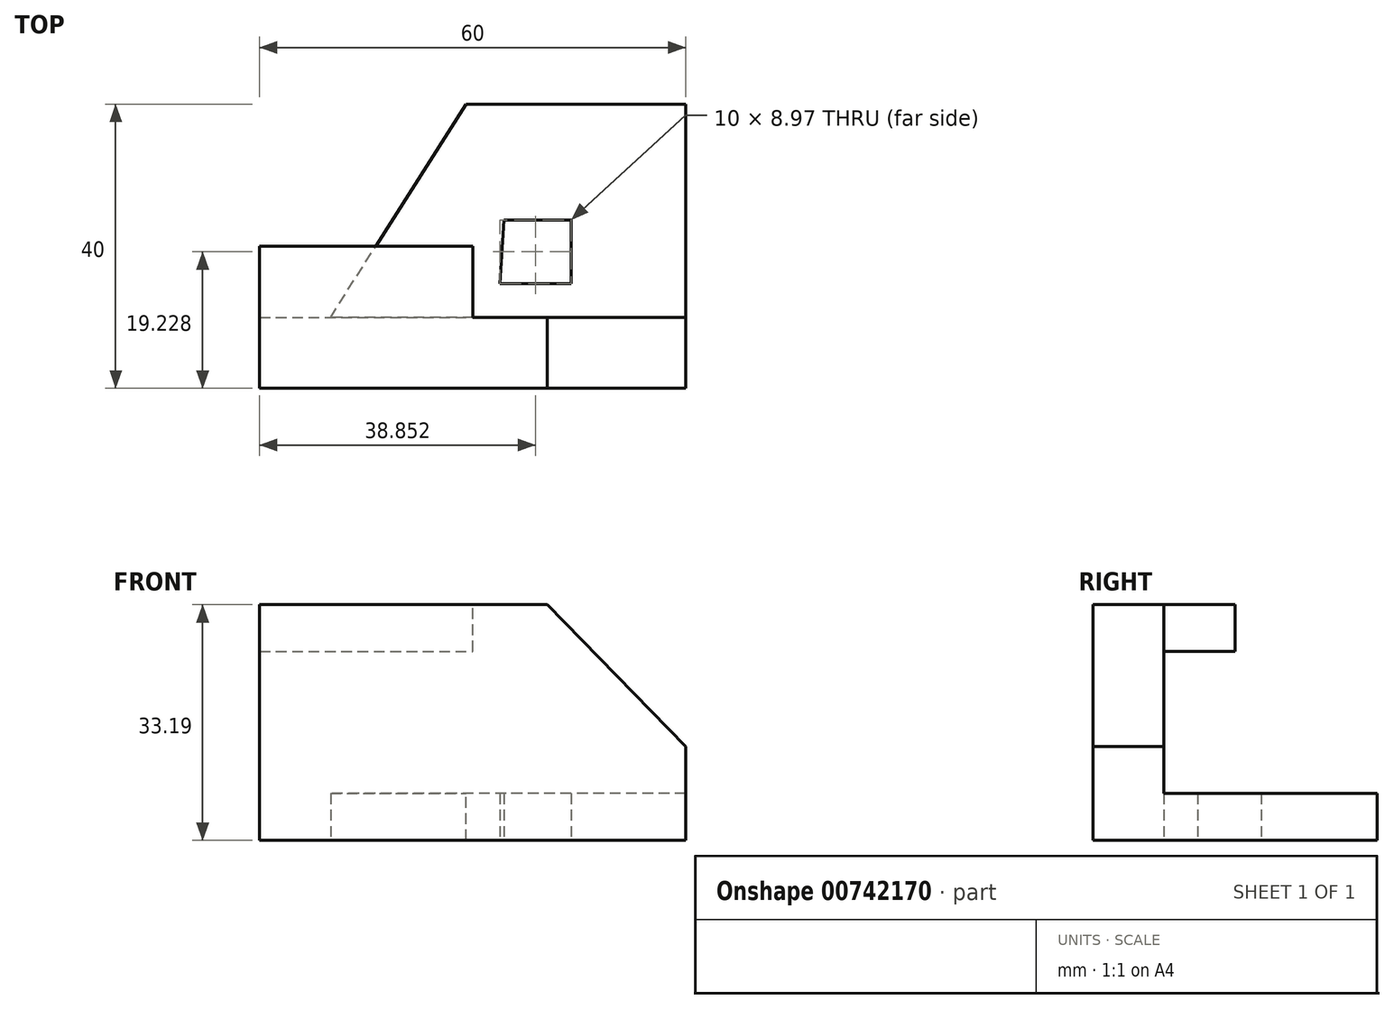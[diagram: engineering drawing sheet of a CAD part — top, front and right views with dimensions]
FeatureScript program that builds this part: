
annotation { "Feature Type Name" : "Feature", "Feature Type Description" : "" }
export const myFeature = defineFeature(function(context is Context, id is Id, definition is map)
    precondition{}
    {
        {
            var Q0;
            Q0=qCreatedBy(makeId("Front.planeOp"),FACE);
            var sketch = newSketch(context, id + "F0", { "sketchPlane" : qUnion([Q0])});
            skLineSegment(sketch, "E0", {"start": v(0, 0) * mm, "end": v(-60, 0) * mm});
            skLineSegment(sketch, "E1", {"start": v(-60, 0) * mm, "end": v(-60, -33.19) * mm});
            skLineSegment(sketch, "E2", {"start": v(-60, -33.19) * mm, "end": v(0, -33.19) * mm});
            skLineSegment(sketch, "E3", {"start": v(0, -33.19) * mm, "end": v(0, 0) * mm});
            skSolve(sketch);
        }
        {
            var Q0;
            Q0=makeQuery(id+"F0.imprint","IMPRINT",FACE,{"disambiguationData":[TD([[makeQuery(id+"F0.imprint","IMPRINT",EDGE,{"derivedFrom":sQuery(id+"F0.wireOp",EDGE,"E0")}),1.0]])]});
            extrude(context, id + "F1", {"entities" : qUnion([Q0]), "depth" : 40 * mm, "offsetDistance" : 25.4 * mm});
        }
        {
            var Q0;
            Q0=qCreatedBy(makeId("Front.planeOp"),FACE);
            var sketch = newSketch(context, id + "F2", { "sketchPlane" : qUnion([Q0])});
            skLineSegment(sketch, "E4", {"start": v(0, 0) * mm, "end": v(-19.51, 0) * mm});
            skLineSegment(sketch, "E5", {"start": v(0, 0) * mm, "end": v(0, -20) * mm});
            skLineSegment(sketch, "E6", {"start": v(-19.51, 0) * mm, "end": v(0, -20) * mm});
            skSolve(sketch);
        }
        {
            var Q0;
            Q0=makeQuery(id+"F2.imprint","IMPRINT",FACE,{"disambiguationData":[TD([[makeQuery(id+"F2.imprint","IMPRINT",EDGE,{"derivedFrom":sQuery(id+"F2.wireOp",EDGE,"E4")}),1.0]])]});
            extrude(context, id + "F3", {"entities" : qUnion([Q0]), "operationType" : NewBodyOperationType.REMOVE, "depth" : 41.9 * mm, "offsetDistance" : 25.4 * mm});
        }
        {
            var Q0;
            Q0=makeQuery(id+"F1.opExtrude","CAP_FACE",FACE,{"disambiguationData":[OSD([sQuery(id+"F0.wireOp",EDGE,"E0"),sQuery(id+"F0.wireOp",EDGE,"E1"),sQuery(id+"F0.wireOp",EDGE,"E2"),sQuery(id+"F0.wireOp",EDGE,"E3")])],"isStart":true});
            var sketch = newSketch(context, id + "F4", { "sketchPlane" : qUnion([Q0])});
            skLineSegment(sketch, "E7", {"start": v(0, -26.6) * mm, "end": v(50, -26.6) * mm});
            skLineSegment(sketch, "E8", {"start": v(50, -26.6) * mm, "end": v(50, -33.19) * mm});
            skLineSegment(sketch, "E9", {"start": v(50, -33.19) * mm, "end": v(60, -33.19) * mm});
            skLineSegment(sketch, "E10", {"start": v(60, -33.19) * mm, "end": v(60, -6.58) * mm});
            skPoint(sketch, "E11.endSnap0", {"position": v(60, -19.89) * mm});
            skLineSegment(sketch, "E12", {"start": v(60, -6.58) * mm, "end": v(30, -6.58) * mm});
            skLineSegment(sketch, "E13", {"start": v(30, -6.58) * mm, "end": v(30, 0) * mm});
            skSolve(sketch);
        }
        {
            var Q0;
            {var subQ2=sQuery(id+"F4.wireOp",EDGE,"E7");Q0=makeQuery(id+"F4.imprint","IMPRINT",FACE,{"disambiguationData":[TD([[makeQuery(id+"F4.imprint","IMPRINT",EDGE,{"derivedFrom":subQ2}),1.0]])]});}
            extrude(context, id + "F5", {"entities" : qUnion([Q0]), "operationType" : NewBodyOperationType.REMOVE, "oppositeDirection" : true, "depth" : 30 * mm, "offsetDistance" : 25.4 * mm});
        }
        {
            var Q0;
            {var subQ0=sQuery(id+"F0.wireOp",EDGE,"E0");var subQ1=sQuery(id+"F0.wireOp",EDGE,"E1");Q0=makeQuery(id+"F5.boolean.opBoolean","SPLIT",FACE,{"disambiguationData":[TD([makeQuery(id+"F1.opExtrude","SWEPT_FACE",FACE,{"disambiguationData":[OSD([subQ0])]})])],"derivedFrom":makeQuery(id+"F1.opExtrude","CAP_FACE",FACE,{"disambiguationData":[OSD([subQ0,subQ1,sQuery(id+"F0.wireOp",EDGE,"E2"),sQuery(id+"F0.wireOp",EDGE,"E3")])],"isStart":true})});}
            extrude(context, id + "F6", {"entities" : qUnion([Q0]), "operationType" : NewBodyOperationType.REMOVE, "oppositeDirection" : true, "depth" : 20 * mm, "offsetDistance" : 25.4 * mm});
        }
        {
            var Q0;
            Q0=makeQuery(id+"F5.boolean.opBoolean","COPY",FACE,{"derivedFrom":makeQuery(id+"F5.opExtrude","SWEPT_FACE",FACE,{"disambiguationData":[OSD([sQuery(id+"F4.wireOp",EDGE,"E7")])]})});
            var sketch = newSketch(context, id + "F7", { "sketchPlane" : qUnion([Q0])});
            skLineSegment(sketch, "E14", {"start": v(-50, -30) * mm, "end": v(-30.92, 0) * mm});
            skLineSegment(sketch, "E15", {"start": v(-50, -30) * mm, "end": v(-50, 0) * mm});
            skLineSegment(sketch, "E16", {"start": v(-50, 0) * mm, "end": v(-30.92, 0) * mm});
            skSolve(sketch);
        }
        {
            var Q0;
            Q0=makeQuery(id+"F7.imprint","IMPRINT",FACE,{"disambiguationData":[TD([[makeQuery(id+"F7.imprint","IMPRINT",EDGE,{"derivedFrom":sQuery(id+"F7.wireOp",EDGE,"E14")}),1.0]])]});
            extrude(context, id + "F8", {"entities" : qUnion([Q0]), "operationType" : NewBodyOperationType.REMOVE, "oppositeDirection" : true, "depth" : 25.4 * mm, "offsetDistance" : 25.4 * mm});
        }
        {
            var Q0;
            Q0=makeQuery(id+"F1.opExtrude","SWEPT_FACE",FACE,{"disambiguationData":[OSD([sQuery(id+"F0.wireOp",EDGE,"E2")])]});
            var sketch = newSketch(context, id + "F9", { "sketchPlane" : qUnion([Q0])});
            skLineSegment(sketch, "E17", {"start": v(-16.15, 16.29) * mm, "end": v(-16.15, 25.26) * mm});
            skLineSegment(sketch, "E18", {"start": v(-16.15, 25.26) * mm, "end": v(-26.15, 25.26) * mm});
            skLineSegment(sketch, "E19", {"start": v(-16.15, 16.29) * mm, "end": v(-25.58, 16.29) * mm});
            skLineSegment(sketch, "E20", {"start": v(-25.58, 16.29) * mm, "end": v(-26.15, 25.26) * mm});
            skSolve(sketch);
        }
        {
            var Q0;
            Q0=makeQuery(id+"F9.imprint","IMPRINT",FACE,{"disambiguationData":[TD([[makeQuery(id+"F9.imprint","IMPRINT",EDGE,{"derivedFrom":sQuery(id+"F9.wireOp",EDGE,"E17")}),1.0]])]});
            extrude(context, id + "F10", {"entities" : qUnion([Q0]), "operationType" : NewBodyOperationType.REMOVE, "oppositeDirection" : true, "depth" : 25.4 * mm, "offsetDistance" : 25.4 * mm});
        }
    });
